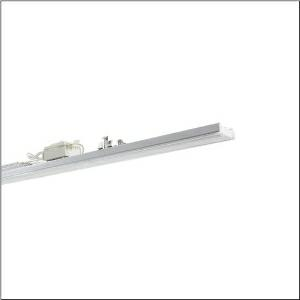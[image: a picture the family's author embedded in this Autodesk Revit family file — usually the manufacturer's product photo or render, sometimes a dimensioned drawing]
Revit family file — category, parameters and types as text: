
# Revit family: licross_21_recessed_mo_52tl12dn68xg3s
name_source: partatom
category: Lighting Fixtures
units: mm (PartAtom-declared; Revit-internal decimal feet)

## family parameters
Cut with Voids When Loaded = No
Host = Face
Light Source = No
Part Type = Normal
Room Calculation Point = No
Round Connector Dimension = Use Diameter
Shared = No

## types (1)
- --- (1 x LED, 920 lm, 6.7 W, 6500K)
    Apparent Load = 7 VA
    CIE Flux Codes = 72 92 99 100 100
    Color Rendering = 80
    Color Temperature = 6500K
    Default Elevation = 1800 mm
    Description = Licross 21 Recessed MO, luminaire insert, of sheet steel, galvanised, coil coated, white, length: 1.500mm, width: 66mm, height: 67mm, LED rated luminous flux: 8.000lm, light colour: 865, SDCM (Standard Deviation of Colour Matching)MacAdam ≤ 3 SDCM (initial), control gear: DALI 2 (for two DALI lines), with plug, 6-pole, with phase selection, for trunking rail, 14-core, mains connection: 220..240V, AC, 50/60Hz, rated input power: 46W, for emergency light function, internal wiring halogen-free, for trunking rail, 14-core, converter,control gear: single battery element, battery: LiFePO4, 9Ah, primary optical cover: cover, of PMMA, light emission: direct distribution, primary light characteristic: symmetric, protection rating (complete): IP40, insulation class (complete): insulation class I (protective earthing), certification: CE, UKCA, protection symbol: D if used in an environment without relevant dust loads with corresponding accessories, impact resistance: IK06, permissible ambient temperature for indoor applications: +5..+35°C, standard: EN 60598-2-22, corresponds to IFS (International Featured Standards) requirements for safety and quality in the food industry, reducing of maximum allowable ambient temperature of 5°C with ceiling mounting, LABS conformity tested according to VDMA 24364:2018-05, The light source and the operating device comply with the requirements of the Ecodesign Regulation (EU) 2019/2020 and are replaceable in accordance with this regulation, packaging unit: 1 piece
    Height = 58 mm
    Lamp = 1 x LED
    Lamp Light Flux = 920 lm
    Lamp Power = 6.7 W
    Lamp count = 1
    Length = 1500 mm
    Luminous efficacy = 137 lm/W
    Manufacturer = Siteco
    ModVariant = No
    Model = 52TL12DN68XG3S
    Mounting Place = Ceiling
    Mounting Type = Pendant
    Number of Poles = 1
    OnlyDefault = Yes
    Power Factor = 1
    Product Name = Licross 21 Recessed MO
    Product group = luminaire insert | ceiling pendant
    ProductGroupID = 901
    Protection Class = Protection class I
    Protection Degree = IP 40
    RLX_Detail_Level = 1
    RLX_Emergency_Light_Flux = 0 lm
    RLX_Emergency_Type = 0
    RLX_Emergency_Type_DB = No
    RlxData = <blob elided: 25185 chars, md5=8273eda1>
    Socket = socket
    Standby Power = 0 W
    System Light Flux = 920 lm
    System Power = 7 W
    Type Comments = : emergency light operation: 3 h
    Type Image = l_1296930.jpg
    URL = http://relux.com
    VarID = @adj_030069
    Voltage = 0 V
    Weight = 0.00 kg
    Width = 66 mm

## geometry (parser evidence)
native form markers: Blend x4, Sweep x13
no freeform markers — native parametric forms only
